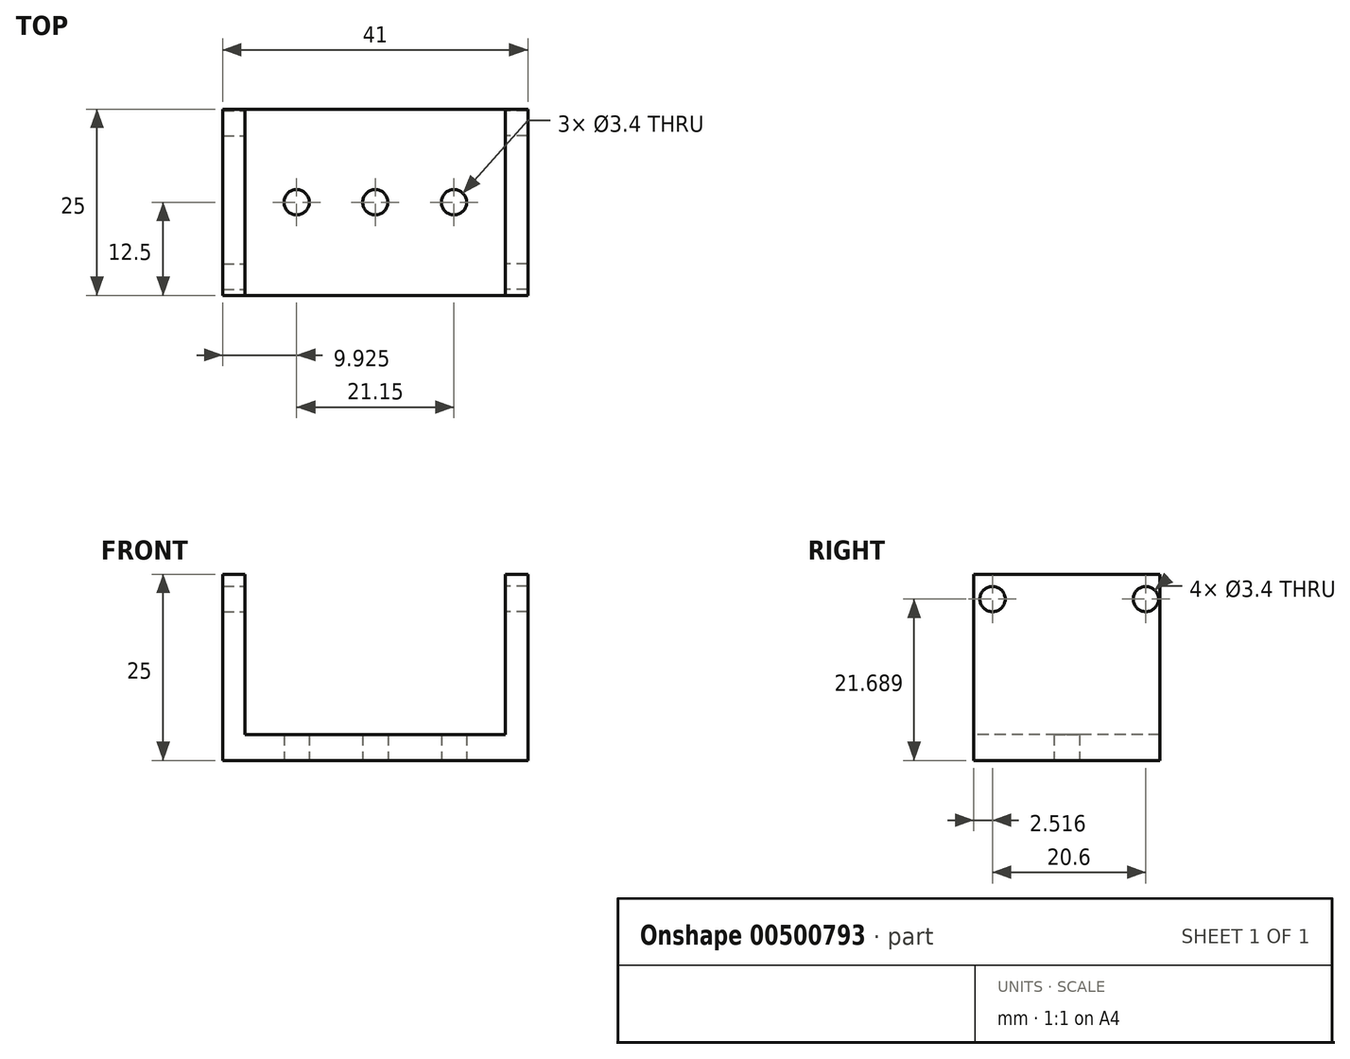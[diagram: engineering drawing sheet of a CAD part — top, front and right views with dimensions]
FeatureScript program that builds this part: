
annotation { "Feature Type Name" : "Feature", "Feature Type Description" : "" }
export const myFeature = defineFeature(function(context is Context, id is Id, definition is map)
    precondition{}
    {
        {
            var Q0;
            Q0=qCreatedBy(makeId("Top.planeOp"),FACE);
            var sketch = newSketch(context, id + "F0", { "sketchPlane" : qUnion([Q0])});
            skLineSegment(sketch, "E0.bottom", {"start": v(17.5, 12.5) * mm, "end": v(-17.5, 12.5) * mm});
            skLineSegment(sketch, "E0.top", {"start": v(17.5, -12.5) * mm, "end": v(-17.5, -12.5) * mm});
            skLineSegment(sketch, "E0.left", {"start": v(17.5, 12.5) * mm, "end": v(17.5, -12.5) * mm});
            skLineSegment(sketch, "E0.right", {"start": v(-17.5, 12.5) * mm, "end": v(-17.5, -12.5) * mm});
            skPoint(sketch, "E0.middle", {"position": v(0, 0) * mm});
            skLineSegment(sketch, "E1", {"start": v(17.5, -12.5) * mm, "end": v(20.5, -12.5) * mm});
            skLineSegment(sketch, "E2", {"start": v(20.5, -12.5) * mm, "end": v(20.5, 12.5) * mm});
            skLineSegment(sketch, "E3", {"start": v(20.5, 12.5) * mm, "end": v(17.5, 12.5) * mm});
            skLineSegment(sketch, "E4", {"start": v(-17.5, 12.5) * mm, "end": v(-20.5, 12.5) * mm});
            skLineSegment(sketch, "E5", {"start": v(-20.5, -12.5) * mm, "end": v(-17.5, -12.5) * mm});
            skLineSegment(sketch, "E6", {"start": v(-20.5, 12.5) * mm, "end": v(-20.5, -12.5) * mm});
            skLineSegment(sketch, "E7", {"start": v(0, 0) * mm, "end": v(-12.32, 0) * mm});
            skLineSegment(sketch, "E8", {"start": v(0, 0) * mm, "end": v(12.32, 0) * mm});
            skLineSegment(sketch, "E9", {"start": v(-12.32, 0) * mm, "end": v(-8.82, 0) * mm});
            skLineSegment(sketch, "E10", {"start": v(12.32, 0) * mm, "end": v(8.82, 0) * mm});
            skCircle(sketch, "E11", {"center": v(0, 0) * mm, "radius": 1.7 * mm});
            skLineSegment(sketch, "E12", {"start": v(-8.82, 0) * mm, "end": v(-10.57, 0) * mm});
            skLineSegment(sketch, "E13", {"start": v(8.82, 0) * mm, "end": v(10.57, 0) * mm});
            skCircle(sketch, "E14", {"center": v(-10.57, 0) * mm, "radius": 1.7 * mm});
            skCircle(sketch, "E15", {"center": v(10.57, 0) * mm, "radius": 1.7 * mm});
            skSolve(sketch);
        }
        {
            var Q0;
            Q0=qCreatedBy(makeId("Right.planeOp"),FACE);
            var sketch = newSketch(context, id + "F1", { "sketchPlane" : qUnion([Q0])});
            skLineSegment(sketch, "E16", {"start": v(12.82, 0) * mm, "end": v(12.82, 25) * mm});
            skLineSegment(sketch, "E17", {"start": v(-12.18, 0) * mm, "end": v(-12.18, 25) * mm});
            skLineSegment(sketch, "E18", {"start": v(-12.18, 25) * mm, "end": v(12.82, 25) * mm});
            skLineSegment(sketch, "E19", {"start": v(12.82, 25) * mm, "end": v(12.82, 21.69) * mm});
            skLineSegment(sketch, "E20", {"start": v(-12.18, 25) * mm, "end": v(-12.18, 21.69) * mm});
            skLineSegment(sketch, "E21", {"start": v(-12.18, 21.69) * mm, "end": v(-9.98, 21.69) * mm});
            skLineSegment(sketch, "E22", {"start": v(12.82, 21.69) * mm, "end": v(10.62, 21.69) * mm});
            skCircle(sketch, "E23", {"center": v(-9.98, 21.69) * mm, "radius": 1.7 * mm});
            skCircle(sketch, "E24", {"center": v(10.62, 21.69) * mm, "radius": 1.7 * mm});
            skSolve(sketch);
        }
        {
            var Q0;
            Q0=makeQuery(id+"F0.imprint","IMPRINT",FACE,{"disambiguationData":[TD([[makeQuery(id+"F0.imprint","IMPRINT",EDGE,{"derivedFrom":sQuery(id+"F0.wireOp",EDGE,"E0.bottom")}),1.0]])]});
            extrude(context, id + "F2", {"entities" : qUnion([Q0]), "depth" : 3.5 * mm, "offsetDistance" : 25 * mm});
        }
        {
            var Q0;
            Q0=makeQuery(id+"F0.imprint","IMPRINT",FACE,{"disambiguationData":[TD([[makeQuery(id+"F0.imprint","IMPRINT",EDGE,{"derivedFrom":sQuery(id+"F0.wireOp",EDGE,"E0.right")}),-1.0]])]});
            extrude(context, id + "F3", {"entities" : qUnion([Q0]), "operationType" : NewBodyOperationType.ADD, "depth" : 25 * mm, "offsetDistance" : 25 * mm});
        }
        {
            var Q0;
            Q0=makeQuery(id+"F0.imprint","IMPRINT",FACE,{"disambiguationData":[TD([[makeQuery(id+"F0.imprint","IMPRINT",EDGE,{"derivedFrom":sQuery(id+"F0.wireOp",EDGE,"E0.left")}),1.0]])]});
            extrude(context, id + "F4", {"entities" : qUnion([Q0]), "operationType" : NewBodyOperationType.ADD, "depth" : 25 * mm, "offsetDistance" : 25 * mm});
        }
        {
            var Q0;
            Q0=sQuery(id+"F1.wireOp",VERTEX,"E21.end");
            var Q1;
            Q1=makeQuery(id+"F2.opExtrude","SWEPT_BODY",BODY,{"disambiguationData":[OSD([sQuery(id+"F0.wireOp",EDGE,"E0.bottom"),sQuery(id+"F0.wireOp",EDGE,"E0.top"),sQuery(id+"F0.wireOp",EDGE,"E0.left"),sQuery(id+"F0.wireOp",EDGE,"E0.right")])]});
            hole(context, id + "F5", {"style" : HoleStyle.SIMPLE, "endStyle" : HoleEndStyle.THROUGH, "oppositeDirection" : true, "holeDiameter" : 3.4 * mm, "isTappedThrough" : true, "tappedDepth" : 12 * mm, "tapClearance" : 3, "locations" : qUnion([Q0]), "scope" : qUnion([Q1])});
        }
        {
            var Q0;
            Q0=sQuery(id+"F1.wireOp",VERTEX,"E22.end");
            var Q1;
            Q1=makeQuery(id+"F2.opExtrude","SWEPT_BODY",BODY,{"disambiguationData":[OSD([sQuery(id+"F0.wireOp",EDGE,"E0.bottom"),sQuery(id+"F0.wireOp",EDGE,"E0.top"),sQuery(id+"F0.wireOp",EDGE,"E0.left"),sQuery(id+"F0.wireOp",EDGE,"E0.right")])]});
            hole(context, id + "F6", {"style" : HoleStyle.SIMPLE, "endStyle" : HoleEndStyle.THROUGH, "oppositeDirection" : true, "holeDiameter" : 3.4 * mm, "isTappedThrough" : true, "tappedDepth" : 12 * mm, "tapClearance" : 3, "locations" : qUnion([Q0]), "scope" : qUnion([Q1])});
        }
        {
            var Q0;
            Q0=sQuery(id+"F1.wireOp",VERTEX,"E21.end");
            var Q1;
            Q1=sQuery(id+"F1.wireOp",VERTEX,"E24.center");
            var Q2;
            Q2=makeQuery(id+"F2.opExtrude","SWEPT_BODY",BODY,{"disambiguationData":[OSD([sQuery(id+"F0.wireOp",EDGE,"E0.bottom"),sQuery(id+"F0.wireOp",EDGE,"E0.top"),sQuery(id+"F0.wireOp",EDGE,"E0.left"),sQuery(id+"F0.wireOp",EDGE,"E0.right")])]});
            hole(context, id + "F7", {"style" : HoleStyle.SIMPLE, "endStyle" : HoleEndStyle.THROUGH, "holeDiameter" : 3.4 * mm, "isTappedThrough" : true, "tappedDepth" : 12 * mm, "tapClearance" : 3, "locations" : qUnion([Q0, Q1]), "scope" : qUnion([Q2])});
        }
    });
